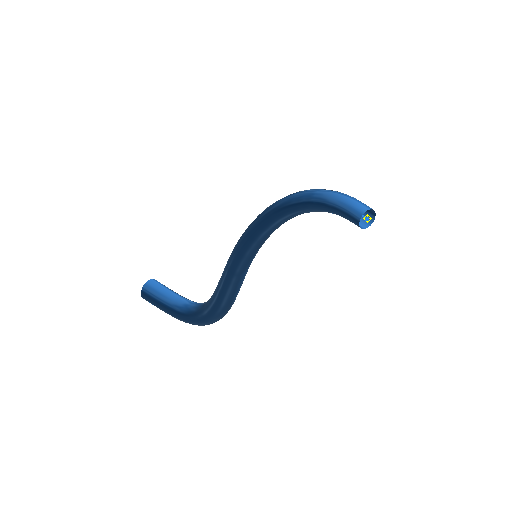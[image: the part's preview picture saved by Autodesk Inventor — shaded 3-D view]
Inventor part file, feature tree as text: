
AUTODESK INVENTOR PART (.ipt)
format: ipt  version: 2022 (Build 260153000, 153)  size: 138,240 bytes
history: native  units: mm (DEFAULTED — no unit token found)
features: other x7, plane x1, sketch x1, sweep x1
ambient origin geometry x8: Origin, YZ Plane, XZ Plane, XY Plane, X Axis, Y Axis, Z Axis, Center Point
bodies: Body1 (feature_tree)
feature tree (10):
  other  "Work Point1"
  other  "Work Point2"
  other  "Wire1"
  other  "Work Point3"
  other  "Work Point4"
  other  "Work Point5"
  plane  "Work Plane1"
  sketch  "Sketch1"  dims[d0=0.0mm d1=0.0mm]
  other  "Srf1"
  sweep  "SweepSrf1"
